# Revit family: PRD_FrankeWS_WlHngWshBsns_RondaWashBasin_ANMW230,231
name_source: partatom
category: Plumbing Fixtures
revit_build: Autodesk Revit 2018 (Build: 20190510_1515(x64)
units: mm (PartAtom-declared; Revit-internal decimal feet)

## family parameters
Cut with Voids When Loaded = No
Host = Face
OmniClass Number = 23.45.05.14.14
OmniClass Title = Sinks/Lavatories
Part Type = Normal
Room Calculation Point = No
Round Connector Dimension = Use Diameter
Shared = No

## types (2) — shared parameters
AssetType = Fixed
BowlOffset = 700 mm  [stored 2.29659 ft]
Category = Pr_40_20_96_96, Wall-hung wash basins
Color = Alpinewhite
Default Elevation = 850 mm  [stored 2.78871 ft]
DrainSize = DN 32 (1 1/4inch)
DurationUnit = year
Features = mineral material, wall mounting, 2100x125x530 mm (WxHxD)
Form = Wall hung wash basin
GrossWeight = 56.70 kg
IfcExportAs = IfcSanitaryTerminalType
IfcExportType = WASHHANDBASIN
IntegralAccessories = Mounting material included (hanger bolts and dowels).
Manufacturer = KWC Group AG
ManufacturerName = KWC Group AG
ManufacturerURL = www.kwc.com
Material = Mineral material
MaterialsBody = Miranit
MaterialsFinishAndColour = Alpinewhite
NBSDescription = Wall hung wash basins
NBSReference = 45-35-70/369
NetWeight = 54.00 kg
NominalDepth = 530 mm  [stored 1.73885 ft]
NominalHeight = 125 mm  [stored 0.410105 ft]
NominalLength = 125 mm  [stored 0.410105 ft]
NominalWidth = 2100 mm  [stored 6.88976 ft]
OverallDepth = 530 mm  [stored 1.73885 ft]
OverallHeight = 125 mm  [stored 0.410105 ft]
OverallWidth = 2100 mm  [stored 6.88976 ft]
ProductInformation = https://pim.kwc.com
Size = 530 x 125 x 2100 mm
StainerMaterial = PRD_AR_StainlessSteel_SatinFinished
URL = www.kwc.com
Uniclass2015Code = Pr_40_20_96_96
Uniclass2015Title = Wall-hung wash basins
Uniclass2015Version = Products v1.7
Version = 1
WarrantyDurationUnit = year
WashHandBasinMounting = WallHung
WashHandBasinType = Other
WashbasinMaterial = PRD_AR_Miranit_Alpinewhite
WasteSize = 32  [stored 0.104987 ft]
WaterSupplyOverflowAndWasteHolesOverflow = None
WaterSupplyOverflowAndWasteHolesWaste = Center-Back

## per-type parameters (varying)
| type | BIMObjectName | Description | Model | ModelNumber | ModelReference | Name | Taphole | WaterSupplyOverflowAndWasteHolesWaterSupply |
| ANMW231 - with tapholes | PRD_AR_WallHungWashBasins_RondaTripleWashBasin_ANMW231 | RONDA triple washbasin made of MIRANIT resin-bonded mineral material with smooth, pore-free surface (temperature-resistant up to 80°C). With three seamless round bowls, flattened out at the rear, without overflow. Integral back panel with integrated brackets and holes for fixing. Rear contoured edge. Three-sided apron. Mounting material included (hanger bolts and dowels). Alpine white colour. Washbasin dimensions 2100 x 60 x 530 (W x H x D), bowl dimensions 540 x 90 x 380 (W x H x D). with tapholes | ANMW231 | 2000090009 | ANMW231 | RONDA triple washbasin ANMW231 | Yes | Single tap hole, centred |
| ANMW230 - without tapholes | PRD_AR_WallHungWashBasins_RondaTripleWashBasin_ANMW230 | RONDA triple washbasin made of MIRANIT resin-bonded mineral material with smooth, pore-free surface (temperature-resistant up to 80°C). With three seamless round bowls, flattened out at the rear, without overflow. Integral back panel with integrated brackets and holes for fixing. Rear contoured edge. Three-sided apron. Mounting material included (hanger bolts and dowels). Alpine white colour. Washbasin dimensions 2100 x 60 x 530 (W x H x D), bowl dimensions 540 x 90 x 380 (W x H x D). without tapholes | ANMW230 | 2000090008 | ANMW230 | RONDA triple washbasin ANMW230 | No | no tapholes |

note: [stored X ft] marks values corroborated as IEEE doubles in the binary element streams (Revit-internal decimal feet)

## geometry (parser evidence)
native form markers: Sweep x11
no freeform markers — native parametric forms only
